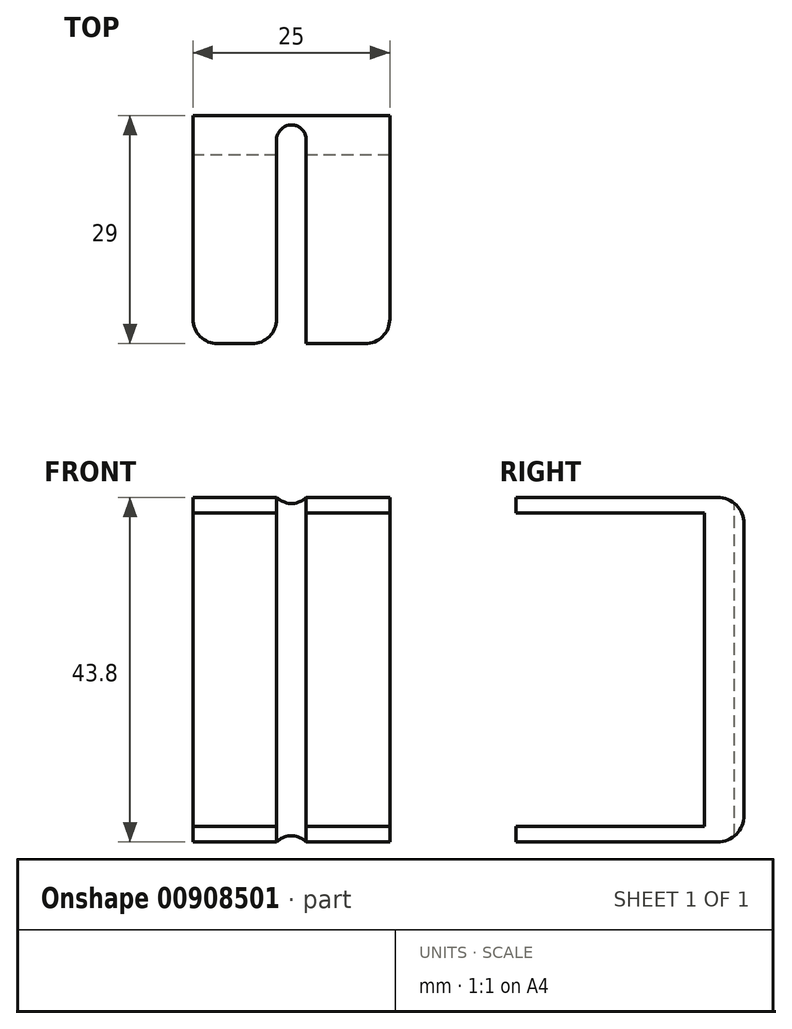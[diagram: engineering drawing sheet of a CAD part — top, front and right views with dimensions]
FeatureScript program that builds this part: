
annotation { "Feature Type Name" : "Feature", "Feature Type Description" : "" }
export const myFeature = defineFeature(function(context is Context, id is Id, definition is map)
    precondition{}
    {
        {
            var Q0;
            Q0=qCreatedBy(makeId("Right.planeOp"),FACE);
            var sketch = newSketch(context, id + "F0", { "sketchPlane" : qUnion([Q0])});
            skLineSegment(sketch, "E0", {"start": v(-29, 43.8) * mm, "end": v(0, 43.8) * mm});
            skLineSegment(sketch, "E1", {"start": v(0, 43.8) * mm, "end": v(0, 0) * mm});
            skLineSegment(sketch, "E2", {"start": v(0, 0) * mm, "end": v(-29, 0) * mm});
            skLineSegment(sketch, "E3", {"start": v(-29, 0) * mm, "end": v(-29, 2) * mm});
            skLineSegment(sketch, "E4", {"start": v(-29, 2) * mm, "end": v(-4, 2) * mm});
            skLineSegment(sketch, "E5", {"start": v(-4, 2) * mm, "end": v(-4, 41.8) * mm});
            skLineSegment(sketch, "E6", {"start": v(-4, 41.8) * mm, "end": v(-29, 41.8) * mm});
            skLineSegment(sketch, "E7", {"start": v(-29, 41.8) * mm, "end": v(-29, 43.8) * mm});
            skSolve(sketch);
        }
        {
            var Q0;
            Q0 = qSketchRegion(id + "F0", true);
            extrude(context, id + "F1", {"entities" : qUnion([Q0]), "depth" : 25 * mm, "offsetDistance" : 25 * mm});
        }
        {
            var Q0;
            Q0=makeQuery(id+"F1.opExtrude","SWEPT_FACE",FACE,{"disambiguationData":[OSD([sQuery(id+"F0.wireOp",EDGE,"E5")])]});
            extrude(context, id + "F2", {"entities" : qUnion([Q0]), "operationType" : NewBodyOperationType.ADD, "depth" : 1 * mm, "offsetDistance" : 25 * mm});
        }
        {
            var Q0;
            Q0=makeQuery(id+"F1.opExtrude","SWEPT_FACE",FACE,{"disambiguationData":[OSD([sQuery(id+"F0.wireOp",EDGE,"E0")])]});
            var sketch = newSketch(context, id + "F3", { "sketchPlane" : qUnion([Q0])});
            skCircle(sketch, "E8", {"center": v(12.5, -3.07) * mm, "radius": 1.88 * mm});
            skLineSegment(sketch, "E9", {"start": v(12.5, -3.07) * mm, "end": v(10.62, -3.07) * mm});
            skLineSegment(sketch, "E10", {"start": v(10.62, -3.07) * mm, "end": v(10.62, -29) * mm});
            skLineSegment(sketch, "E11", {"start": v(12.5, -3.07) * mm, "end": v(14.38, -3.07) * mm});
            skLineSegment(sketch, "E12", {"start": v(14.38, -3.07) * mm, "end": v(14.38, -29) * mm});
            skLineSegment(sketch, "E13", {"start": v(14.38, -29) * mm, "end": v(10.62, -29) * mm});
            skSolve(sketch);
        }
        {
            var Q0;
            Q0 = qSketchRegion(id + "F3", true);
            extrude(context, id + "F4", {"entities" : qUnion([Q0]), "operationType" : NewBodyOperationType.REMOVE, "oppositeDirection" : true, "depth" : 47.5 * mm, "offsetDistance" : 25 * mm});
        }
        {
            var Q0;
            Q0=makeQuery(id+"F1.opExtrude","CAP_EDGE",EDGE,{"disambiguationData":[OSD([sQuery(id+"F0.wireOp",EDGE,"E7")])],"isStart":true});
            var Q1;
            {var subQ0=sQuery(id+"F0.wireOp",EDGE,"E7");var subQ1=sQuery(id+"F3.wireOp",EDGE,"E10");Q1=makeQuery(id+"F4.boolean.opBoolean","COPY",EDGE,{"disambiguationData":[topologyDisambiguationEdgeConnected([makeQuery(id+"F1.opExtrude","SWEPT_FACE",FACE,{"disambiguationData":[OSD([subQ0])]})])],"derivedFrom":makeQuery(id+"F4.opExtrude","SWEPT_EDGE",EDGE,{"disambiguationData":[OSD([sQuery(id+"F0.wireOp",EDGE,"E0"),subQ0,subQ1,sQuery(id+"F3.wireOp",EDGE,"E13")])]})});}
            var Q2;
            {var subQ0=sQuery(id+"F0.wireOp",EDGE,"E7");var subQ1=sQuery(id+"F3.wireOp",EDGE,"E12");Q2=makeQuery(id+"F4.boolean.opBoolean","COPY",EDGE,{"disambiguationData":[topologyDisambiguationEdgeConnected([makeQuery(id+"F1.opExtrude","SWEPT_FACE",FACE,{"disambiguationData":[OSD([subQ0])]})])],"derivedFrom":makeQuery(id+"F4.opExtrude","SWEPT_EDGE",EDGE,{"disambiguationData":[OSD([sQuery(id+"F0.wireOp",EDGE,"E0"),subQ0,subQ1,sQuery(id+"F3.wireOp",EDGE,"E13")])]})});}
            var Q3;
            Q3=makeQuery(id+"F1.opExtrude","CAP_EDGE",EDGE,{"disambiguationData":[OSD([sQuery(id+"F0.wireOp",EDGE,"E7")])],"isStart":false});
            var Q4;
            Q4=makeQuery(id+"F1.opExtrude","CAP_EDGE",EDGE,{"disambiguationData":[OSD([sQuery(id+"F0.wireOp",EDGE,"E3")])],"isStart":false});
            var Q5;
            {var subQ0=sQuery(id+"F3.wireOp",EDGE,"E12");Q5=makeQuery(id+"F4.boolean.opBoolean","COPY",EDGE,{"disambiguationData":[topologyDisambiguationEdgeConnected([makeQuery(id+"F1.opExtrude","SWEPT_FACE",FACE,{"disambiguationData":[OSD([sQuery(id+"F0.wireOp",EDGE,"E3")])]})])],"derivedFrom":makeQuery(id+"F4.opExtrude","SWEPT_EDGE",EDGE,{"disambiguationData":[OSD([sQuery(id+"F0.wireOp",EDGE,"E0"),sQuery(id+"F0.wireOp",EDGE,"E7"),subQ0,sQuery(id+"F3.wireOp",EDGE,"E13")])]})});}
            var Q6;
            {var subQ0=sQuery(id+"F3.wireOp",EDGE,"E10");Q6=makeQuery(id+"F4.boolean.opBoolean","COPY",EDGE,{"disambiguationData":[topologyDisambiguationEdgeConnected([makeQuery(id+"F1.opExtrude","SWEPT_FACE",FACE,{"disambiguationData":[OSD([sQuery(id+"F0.wireOp",EDGE,"E3")])]})])],"derivedFrom":makeQuery(id+"F4.opExtrude","SWEPT_EDGE",EDGE,{"disambiguationData":[OSD([sQuery(id+"F0.wireOp",EDGE,"E0"),sQuery(id+"F0.wireOp",EDGE,"E7"),subQ0,sQuery(id+"F3.wireOp",EDGE,"E13")])]})});}
            var Q7;
            Q7=makeQuery(id+"F1.opExtrude","CAP_EDGE",EDGE,{"disambiguationData":[OSD([sQuery(id+"F0.wireOp",EDGE,"E3")])],"isStart":true});
            fillet(context, id + "F5", {"entities" : qUnion([Q0, Q1, Q2, Q3, Q4, Q5, Q6, Q7]), "radius" : 3.14 * mm, "tangentPropagation" : true, "allowEdgeOverflow" : false});
        }
        {
            var Q0;
            Q0=makeQuery(id+"F1.opExtrude","SWEPT_EDGE",EDGE,{"disambiguationData":[OSD([sQuery(id+"F0.wireOp",EDGE,"E0"),sQuery(id+"F0.wireOp",EDGE,"E1")])]});
            var Q1;
            Q1=makeQuery(id+"F1.opExtrude","SWEPT_EDGE",EDGE,{"disambiguationData":[OSD([sQuery(id+"F0.wireOp",EDGE,"E1"),sQuery(id+"F0.wireOp",EDGE,"E2")])]});
            fillet(context, id + "F6", {"entities" : qUnion([Q0, Q1]), "radius" : 3.38 * mm, "tangentPropagation" : true, "allowEdgeOverflow" : false});
        }
    });
